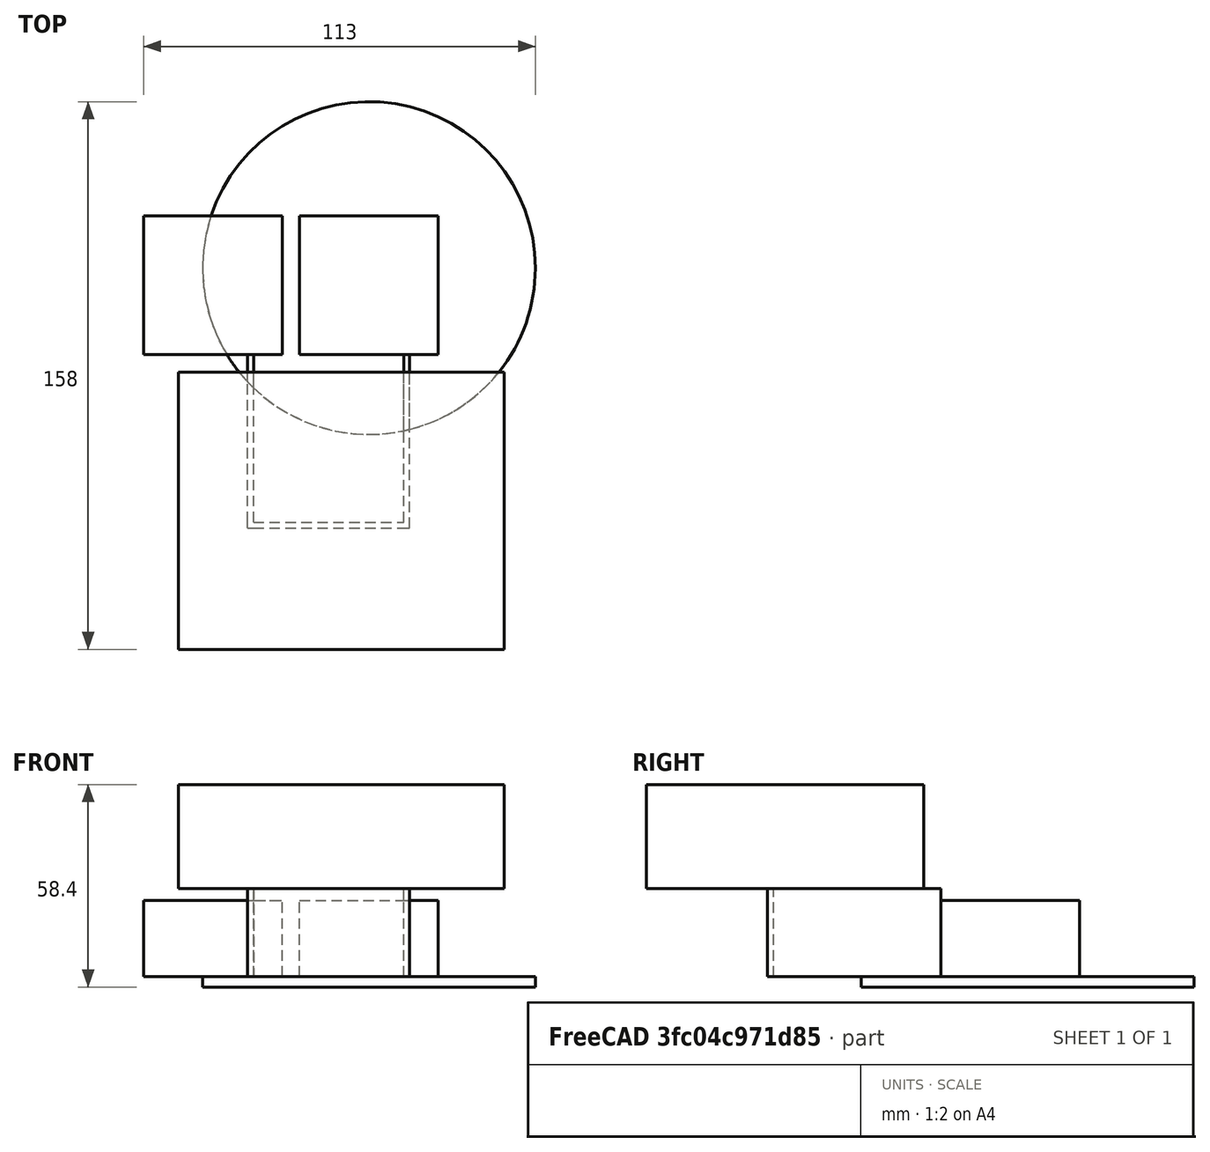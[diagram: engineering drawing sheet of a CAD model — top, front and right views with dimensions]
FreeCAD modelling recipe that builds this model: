
FCSTD DOCUMENT
Label: Shoulder
objects: Part::Box×6, Part::MultiFuse×2, Part::Cylinder×1
note: 9 computed .brp shape members not serialized (recipe doc carries the construction recipe); baked Part::Feature solids carry a one-line shape summary decoded from their .brp

FEATURE [Part::Cylinder] Cylinder  label="Base"
  Angle = 360
  Height = 3
  Radius = 48
FEATURE [Part::Box] Box  label="Servo 1a"
  Height = 22
  Length = 40
  Placement = pos=(-20,-25,3) rot=(0,0,1;0rad)
  Width = 40
FEATURE [Part::Box] Box001  label="Servo 1b"
  Height = 22
  Length = 40
  Placement = pos=(-65,-25,3) rot=(0,0,1;0rad)
  Width = 40
FEATURE [Part::Box] Box002
  Height = 25.4
  Length = 1.7
  Placement = pos=(-35,-75,3) rot=(0,0,1;0rad)
  Width = 50
FEATURE [Part::Box] Box003
  Height = 25.4
  Length = 1.7
  Placement = pos=(10,-75,3) rot=(0,0,1;0rad)
  Width = 50
FEATURE [Part::Box] Box004
  Height = 25.4
  Length = 45
  Placement = pos=(-35,-75,3) rot=(0,0,1;0rad)
  Width = 1.7
FEATURE [Part::MultiFuse] Fusion  label="Counter Weight Support"
  Shapes = -> [Box004,Box002,Box003]
FEATURE [Part::Box] Box005  label="Counter Weight"
  Height = 30
  Length = 94
  Placement = pos=(-55,-110,28.4) rot=(0,0,1;0rad)
  Width = 80
FEATURE [Part::MultiFuse] Fusion001  label="Shoulder"
  Shapes = -> [Cylinder,Box,Box001,Fusion,Box005]
